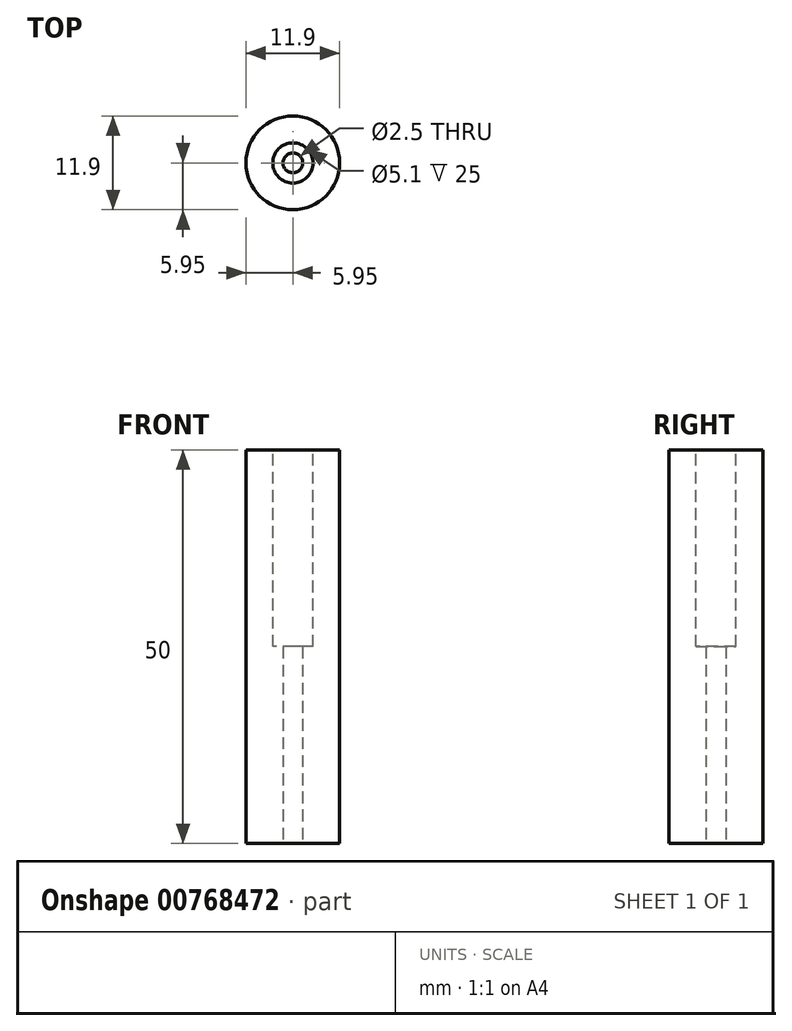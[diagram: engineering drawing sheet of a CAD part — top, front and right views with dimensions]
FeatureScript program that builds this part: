
annotation { "Feature Type Name" : "Feature", "Feature Type Description" : "" }
export const myFeature = defineFeature(function(context is Context, id is Id, definition is map)
    precondition{}
    {
        {
            var Q0;
            Q0=qCreatedBy(makeId("Top.planeOp"),FACE);
            var sketch = newSketch(context, id + "F0", { "sketchPlane" : qUnion([Q0])});
            skCircle(sketch, "E0", {"center": v(0, 0) * mm, "radius": 5.95 * mm});
            skSolve(sketch);
        }
        {
            var Q0;
            Q0=makeQuery(id+"F0.imprint","IMPRINT",FACE,{"disambiguationData":[TD([[makeQuery(id+"F0.imprint","IMPRINT",EDGE,{"derivedFrom":sQuery(id+"F0.wireOp",EDGE,"E0")}),1.0]])]});
            extrude(context, id + "F1", {"entities" : qUnion([Q0]), "depth" : 50 * mm, "offsetDistance" : 25 * mm});
        }
        {
            var Q0;
            Q0=makeQuery(id+"F1.opExtrude","CAP_FACE",FACE,{"disambiguationData":[OSD([sQuery(id+"F0.wireOp",EDGE,"E0")])],"isStart":true});
            var sketch = newSketch(context, id + "F2", { "sketchPlane" : qUnion([Q0])});
            skPoint(sketch, "E1", {"position": v(0, 0) * mm});
            skSolve(sketch);
        }
        {
            var Q0;
            Q0=sQuery(id+"F2.wireOp",VERTEX,"E1");
            var Q1;
            Q1=makeQuery(id+"F1.opExtrude","SWEPT_BODY",BODY,{"disambiguationData":[OSD([sQuery(id+"F0.wireOp",EDGE,"E0")])]});
            hole(context, id + "F3", {"style" : HoleStyle.SIMPLE, "endStyle" : HoleEndStyle.THROUGH, "standardTappedOrClearance" : lookupTablePath({ "standard" : "ISO", "engagement" : "75%", "pitch" : "0.5 mm", "size" : "M3", "type" : "Tapped" }), "standardBlindInLast" : lookupTablePath({ "standard" : "ISO", "fit" : "Normal", "engagement" : "75%", "pitch" : "0.5 mm", "size" : "M3", "type" : "Clearance & tapped" }), "holeDiameter" : 2.5 * mm, "majorDiameter" : 3 * mm, "showTappedDepth" : true, "isTappedThrough" : true, "tappedDepth" : 12 * mm, "tapClearance" : 3, "locations" : qUnion([Q0]), "scope" : qUnion([Q1])});
        }
        {
            var Q0;
            Q0=makeQuery(id+"F1.opExtrude","CAP_FACE",FACE,{"disambiguationData":[OSD([sQuery(id+"F0.wireOp",EDGE,"E0")])],"isStart":false});
            var sketch = newSketch(context, id + "F4", { "sketchPlane" : qUnion([Q0])});
            skPoint(sketch, "E2", {"position": v(0, 0) * mm});
            skCircle(sketch, "E3", {"center": v(0, 0) * mm, "radius": 2.55 * mm});
            skSolve(sketch);
        }
        {
            var Q0;
            Q0=makeQuery(id+"F4.imprint","IMPRINT",FACE,{"disambiguationData":[TD([[makeQuery(id+"F4.imprint","IMPRINT",EDGE,{"derivedFrom":sQuery(id+"F4.wireOp",EDGE,"E3")}),1.0]])]});
            extrude(context, id + "F5", {"entities" : qUnion([Q0]), "operationType" : NewBodyOperationType.REMOVE, "oppositeDirection" : true, "depth" : 25 * mm, "offsetDistance" : 25 * mm});
        }
    });
